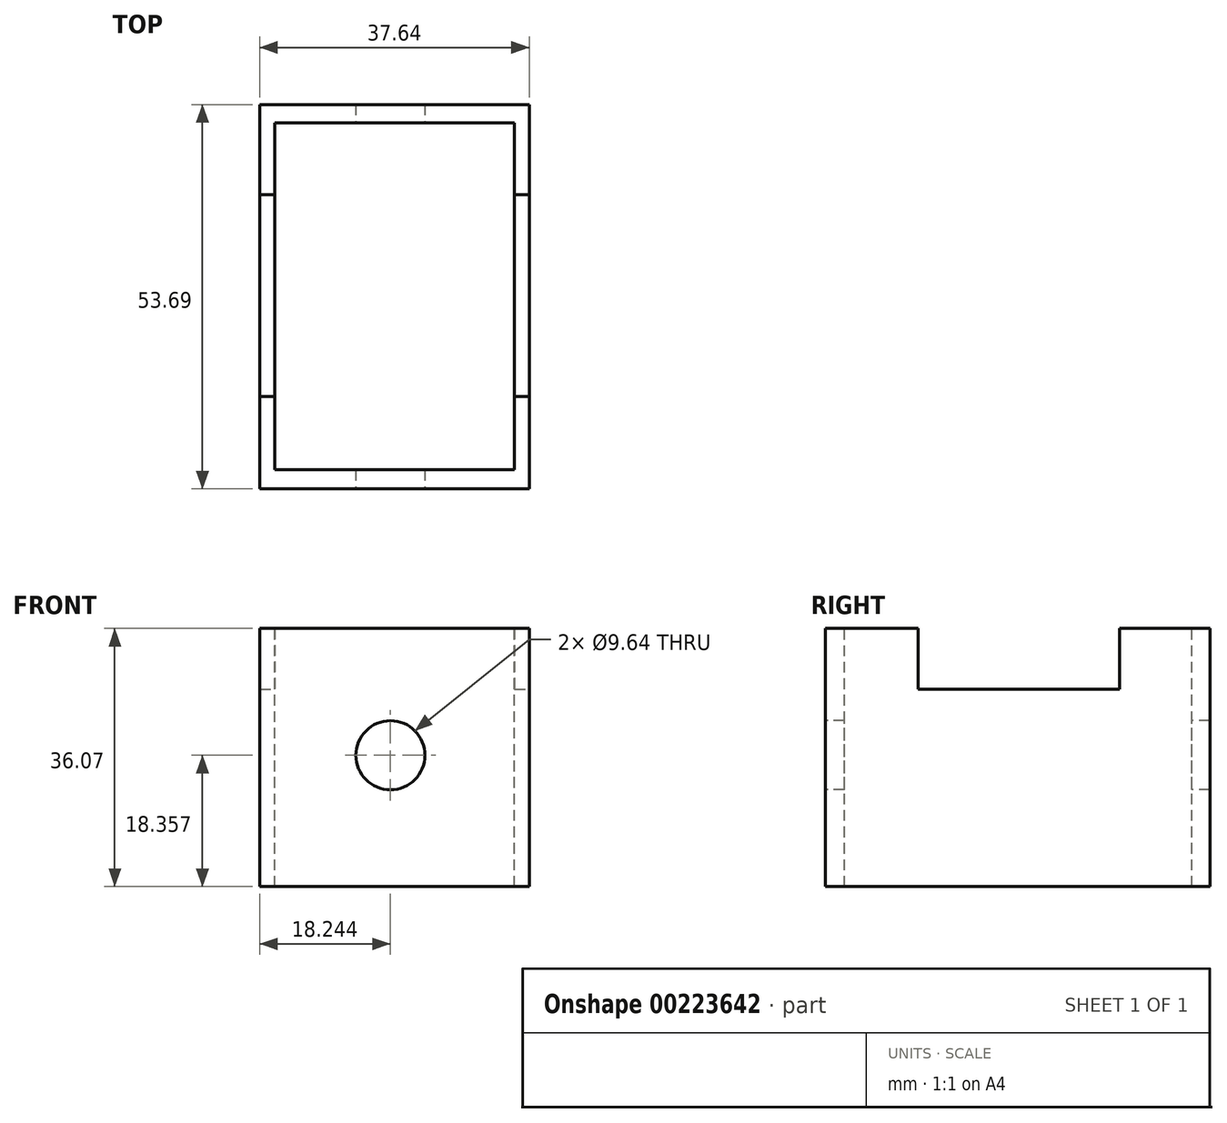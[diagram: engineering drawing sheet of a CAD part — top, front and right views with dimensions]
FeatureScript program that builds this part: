
annotation { "Feature Type Name" : "Feature", "Feature Type Description" : "" }
export const myFeature = defineFeature(function(context is Context, id is Id, definition is map)
    precondition{}
    {
        {
            var Q0;
            Q0=qCreatedBy(makeId("Top.planeOp"),FACE);
            var sketch = newSketch(context, id + "F0", { "sketchPlane" : qUnion([Q0])});
            skLineSegment(sketch, "E0.bottom", {"start": v(0, 0) * mm, "end": v(-37.64, 0) * mm});
            skLineSegment(sketch, "E0.top", {"start": v(0, 53.69) * mm, "end": v(-37.64, 53.69) * mm});
            skLineSegment(sketch, "E0.left", {"start": v(0, 0) * mm, "end": v(0, 53.69) * mm});
            skLineSegment(sketch, "E0.right", {"start": v(-37.64, 0) * mm, "end": v(-37.64, 53.69) * mm});
            skSolve(sketch);
        }
        {
            var Q0;
            Q0=makeQuery(id+"F0.imprint","IMPRINT",FACE,{"disambiguationData":[TD([[makeQuery(id+"F0.imprint","IMPRINT",EDGE,{"derivedFrom":sQuery(id+"F0.wireOp",EDGE,"E0.bottom")}),-1.0]])]});
            extrude(context, id + "F1", {"entities" : qUnion([Q0]), "depth" : 36.07 * mm});
        }
        {
            var Q0;
            Q0=makeQuery(id+"F1.opExtrude","CAP_FACE",FACE,{"disambiguationData":[OSD([sQuery(id+"F0.wireOp",EDGE,"E0.bottom"),sQuery(id+"F0.wireOp",EDGE,"E0.top"),sQuery(id+"F0.wireOp",EDGE,"E0.left"),sQuery(id+"F0.wireOp",EDGE,"E0.right")])],"isStart":false});
            var sketch = newSketch(context, id + "F2", { "sketchPlane" : qUnion([Q0])});
            skLineSegment(sketch, "E1.bottom", {"start": v(-35.56, 2.66) * mm, "end": v(-2.08, 2.66) * mm});
            skLineSegment(sketch, "E1.top", {"start": v(-35.56, 51.15) * mm, "end": v(-2.08, 51.15) * mm});
            skLineSegment(sketch, "E1.left", {"start": v(-35.56, 2.66) * mm, "end": v(-35.56, 51.15) * mm});
            skLineSegment(sketch, "E1.right", {"start": v(-2.08, 2.66) * mm, "end": v(-2.08, 51.15) * mm});
            skSolve(sketch);
        }
        {
            var Q0;
            Q0=makeQuery(id+"F2.imprint","IMPRINT",FACE,{"disambiguationData":[TD([[makeQuery(id+"F2.imprint","IMPRINT",EDGE,{"derivedFrom":sQuery(id+"F2.wireOp",EDGE,"E1.bottom")}),1.0]])]});
            extrude(context, id + "F3", {"entities" : qUnion([Q0]), "operationType" : NewBodyOperationType.REMOVE, "oppositeDirection" : true, "depth" : 49.53 * mm});
        }
        {
            var Q0;
            Q0=makeQuery(id+"F1.opExtrude","SWEPT_FACE",FACE,{"disambiguationData":[OSD([sQuery(id+"F0.wireOp",EDGE,"E0.left")])]});
            var sketch = newSketch(context, id + "F4", { "sketchPlane" : qUnion([Q0])});
            skLineSegment(sketch, "E2", {"start": v(12.93, 36.07) * mm, "end": v(12.93, 27.6) * mm});
            skLineSegment(sketch, "E3", {"start": v(12.93, 27.6) * mm, "end": v(41.1, 27.6) * mm});
            skLineSegment(sketch, "E4", {"start": v(41.1, 27.6) * mm, "end": v(41.1, 36.07) * mm});
            skLineSegment(sketch, "E5", {"start": v(41.1, 36.07) * mm, "end": v(12.93, 36.07) * mm});
            skSolve(sketch);
        }
        {
            var Q0;
            Q0=makeQuery(id+"F4.imprint","IMPRINT",FACE,{"disambiguationData":[TD([[makeQuery(id+"F4.imprint","IMPRINT",EDGE,{"derivedFrom":sQuery(id+"F4.wireOp",EDGE,"E2")}),1.0]])]});
            extrude(context, id + "F5", {"entities" : qUnion([Q0]), "operationType" : NewBodyOperationType.REMOVE, "oppositeDirection" : true, "depth" : 90.17 * mm});
        }
        {
            var Q0;
            Q0=makeQuery(id+"F1.opExtrude","SWEPT_FACE",FACE,{"disambiguationData":[OSD([sQuery(id+"F0.wireOp",EDGE,"E0.bottom")])]});
            var sketch = newSketch(context, id + "F6", { "sketchPlane" : qUnion([Q0])});
            skCircle(sketch, "E6", {"center": v(-19.4, 18.36) * mm, "radius": 4.82 * mm});
            skSolve(sketch);
        }
        {
            var Q0;
            Q0=makeQuery(id+"F6.imprint","IMPRINT",FACE,{"disambiguationData":[TD([[makeQuery(id+"F6.imprint","IMPRINT",EDGE,{"derivedFrom":sQuery(id+"F6.wireOp",EDGE,"E6")}),1.0]])]});
            extrude(context, id + "F7", {"entities" : qUnion([Q0]), "operationType" : NewBodyOperationType.REMOVE, "oppositeDirection" : true, "depth" : 119.13 * mm});
        }
    });
